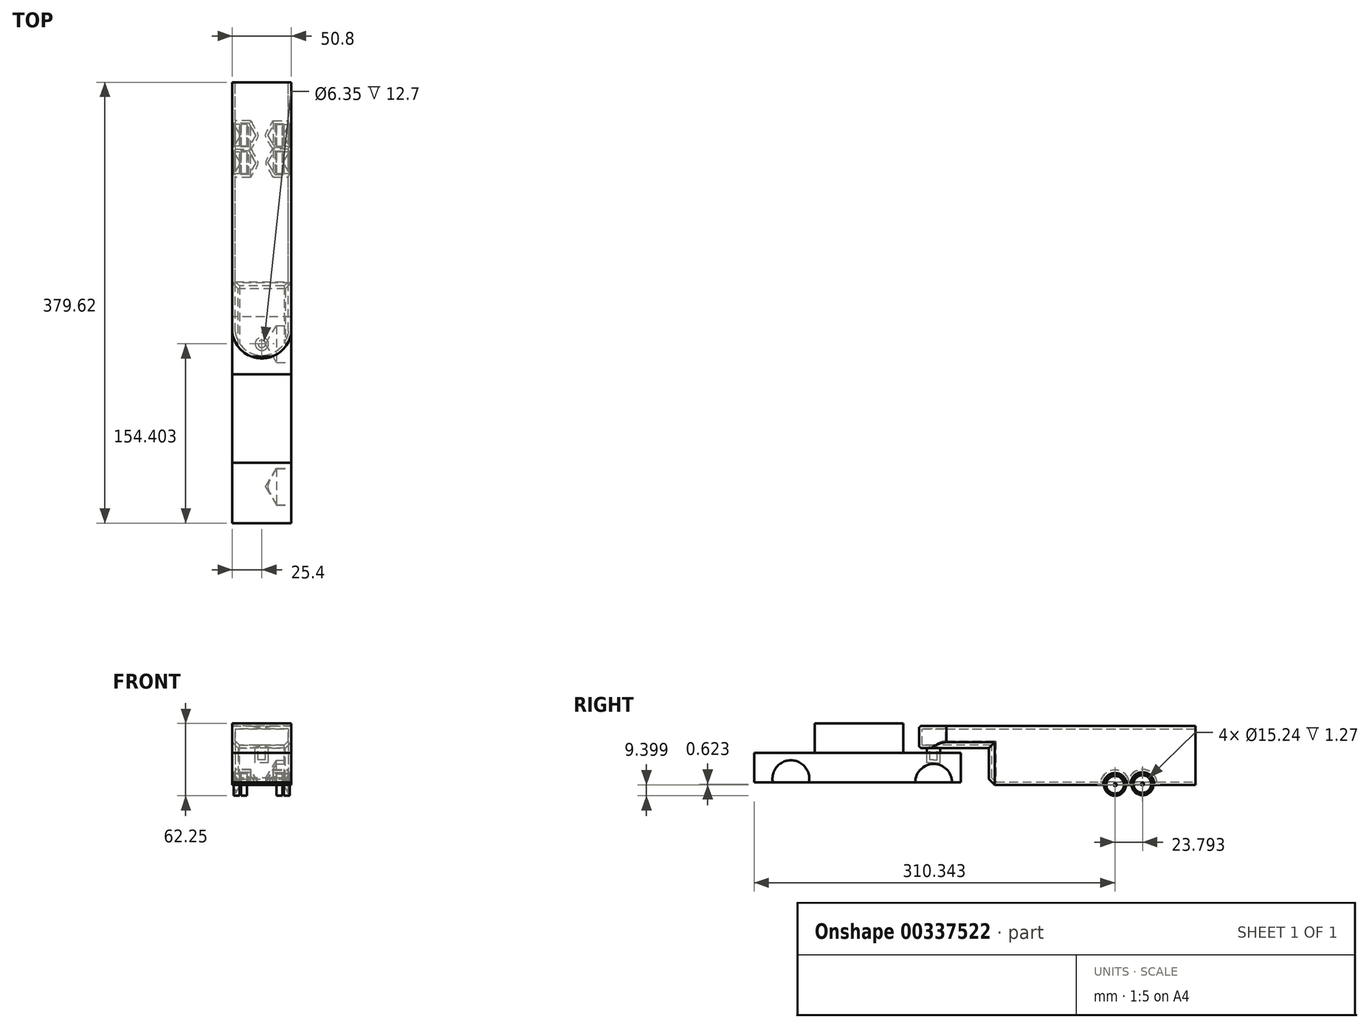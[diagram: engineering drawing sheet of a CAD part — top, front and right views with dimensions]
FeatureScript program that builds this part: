
annotation { "Feature Type Name" : "Feature", "Feature Type Description" : "" }
export const myFeature = defineFeature(function(context is Context, id is Id, definition is map)
    precondition{}
    {
        {
            var Q0;
            Q0=qCreatedBy(makeId("Right.planeOp"),FACE);
            var sketch = newSketch(context, id + "F0", { "sketchPlane" : qUnion([Q0])});
            skLineSegment(sketch, "E0.bottom", {"start": v(-60.47, 27.02) * mm, "end": v(117.33, 27.02) * mm});
            skLineSegment(sketch, "E0.top", {"start": v(-60.47, -23.78) * mm, "end": v(117.33, -23.78) * mm});
            skLineSegment(sketch, "E0.left", {"start": v(-60.47, 27.02) * mm, "end": v(-60.47, -23.78) * mm});
            skLineSegment(sketch, "E0.right", {"start": v(117.33, 27.02) * mm, "end": v(117.33, -23.78) * mm});
            skSolve(sketch);
        }
        {
            var Q0;
            Q0 = qSketchRegion(id + "F0", true);
            extrude(context, id + "F1", {"entities" : qUnion([Q0]), "endBound" : BoundingType.SYMMETRIC, "depth" : 50.8 * mm});
        }
        {
            var Q0;
            Q0=makeQuery(id+"F1.opExtrude","SWEPT_FACE",FACE,{"disambiguationData":[OSD([sQuery(id+"F0.wireOp",EDGE,"E0.bottom")])]});
            var sketch = newSketch(context, id + "F2", { "sketchPlane" : qUnion([Q0])});
            skLineSegment(sketch, "E1", {"start": v(25.4, -60.47) * mm, "end": v(25.4, -123.97) * mm});
            skLineSegment(sketch, "E2", {"start": v(25.4, -123.97) * mm, "end": v(-25.4, -123.97) * mm});
            skLineSegment(sketch, "E3", {"start": v(-25.4, -123.97) * mm, "end": v(-25.4, -60.47) * mm});
            skLineSegment(sketch, "E4", {"start": v(-25.4, -60.47) * mm, "end": v(25.4, -60.47) * mm});
            skSolve(sketch);
        }
        {
            var Q0;
            Q0 = qSketchRegion(id + "F2", true);
            extrude(context, id + "F3", {"entities" : qUnion([Q0]), "operationType" : NewBodyOperationType.ADD, "oppositeDirection" : true, "depth" : 19.05 * mm});
        }
        {
            var Q0;
            Q0=makeQuery(id+"F3.opExtrude","CAP_FACE",FACE,{"disambiguationData":[OSD([sQuery(id+"F2.wireOp",EDGE,"E1"),sQuery(id+"F2.wireOp",EDGE,"E2"),sQuery(id+"F2.wireOp",EDGE,"E3"),sQuery(id+"F2.wireOp",EDGE,"E4")])],"isStart":false});
            var sketch = newSketch(context, id + "F4", { "sketchPlane" : qUnion([Q0])});
            skCircle(sketch, "E5", {"center": v(0, 107.89) * mm, "radius": 5.72 * mm});
            skPoint(sketch, "E5.centerSnap0", {"position": v(25.4, 92.22) * mm});
            skPoint(sketch, "E5.centerSnap1", {"position": v(0, 60.47) * mm});
            skSolve(sketch);
        }
        {
            var Q0;
            Q0 = qSketchRegion(id + "F4", true);
            extrude(context, id + "F5", {"entities" : qUnion([Q0]), "operationType" : NewBodyOperationType.ADD, "depth" : 12.7 * mm});
        }
        {
            var Q0;
            Q0=makeQuery(id+"F3.opExtrude","SWEPT_EDGE",EDGE,{"disambiguationData":[OSD([sQuery(id+"F2.wireOp",EDGE,"E1"),sQuery(id+"F2.wireOp",EDGE,"E2")])]});
            var Q1;
            Q1=makeQuery(id+"F3.opExtrude","SWEPT_EDGE",EDGE,{"disambiguationData":[OSD([sQuery(id+"F2.wireOp",EDGE,"E2"),sQuery(id+"F2.wireOp",EDGE,"E3")])]});
            var Q2;
            Q2=makeQuery(id+"F1.opExtrude","CAP_EDGE",EDGE,{"disambiguationData":[OSD([sQuery(id+"F0.wireOp",EDGE,"E0.left")])],"isStart":false});
            var Q3;
            Q3=makeQuery(id+"F3.opExtrude","CAP_EDGE",EDGE,{"disambiguationData":[OSD([sQuery(id+"F2.wireOp",EDGE,"E1")])],"isStart":false});
            var Q4;
            Q4=makeQuery(id+"F3.opExtrude","CAP_EDGE",EDGE,{"disambiguationData":[OSD([sQuery(id+"F2.wireOp",EDGE,"E3")])],"isStart":false});
            var Q5;
            Q5=makeQuery(id+"F1.opExtrude","CAP_EDGE",EDGE,{"disambiguationData":[OSD([sQuery(id+"F0.wireOp",EDGE,"E0.left")])],"isStart":true});
            var Q6;
            Q6=makeQuery(id+"F1.opExtrude","SWEPT_EDGE",EDGE,{"disambiguationData":[OSD([sQuery(id+"F0.wireOp",EDGE,"E0.top"),sQuery(id+"F0.wireOp",EDGE,"E0.left")])]});
            var Q7;
            Q7=makeQuery(id+"F3.opExtrude","CAP_EDGE",EDGE,{"disambiguationData":[OSD([sQuery(id+"F2.wireOp",EDGE,"E2")])],"isStart":true});
            var Q8;
            Q8=makeQuery(id+"F3.opExtrude","SWEPT_FACE",FACE,{"disambiguationData":[OSD([sQuery(id+"F2.wireOp",EDGE,"E2")])]});
            chamfer(context, id + "F6", {"entities" : qUnion([Q0, Q1, Q2, Q3, Q4, Q5, Q6, Q7, Q8]), "width" : 5.08 * mm, "tangentPropagation" : true});
        }
        {
            var Q0;
            Q0=makeQuery(id+"F5.opExtrude","CAP_FACE",FACE,{"disambiguationData":[OSD([sQuery(id+"F4.wireOp",EDGE,"E5")])],"isStart":false});
            var sketch = newSketch(context, id + "F7", { "sketchPlane" : qUnion([Q0])});
            skCircle(sketch, "E6", {"center": v(0, 107.89) * mm, "radius": 2.54 * mm});
            skSolve(sketch);
        }
        {
            var Q0;
            Q0=makeQuery(id+"F3.boolean.opBoolean","MERGE",FACE,{"derivedFrom":[makeQuery(id+"F1.opExtrude","CAP_FACE",FACE,{"disambiguationData":[OSD([sQuery(id+"F0.wireOp",EDGE,"E0.bottom"),sQuery(id+"F0.wireOp",EDGE,"E0.top"),sQuery(id+"F0.wireOp",EDGE,"E0.left"),sQuery(id+"F0.wireOp",EDGE,"E0.right")])],"isStart":false}),makeQuery(id+"F3.opExtrude","SWEPT_FACE",FACE,{"disambiguationData":[OSD([sQuery(id+"F2.wireOp",EDGE,"E1")])]})]});
            var sketch = newSketch(context, id + "F8", { "sketchPlane" : qUnion([Q0])});
            skArc(sketch, "E7", {"start": v(57.9, -23.78) * mm, "mid": v(48.24, -14.02) * mm, "end": v(38.59, -23.78) * mm});
            skArc(sketch, "E8", {"start": v(81.4, -23.78) * mm, "mid": v(71.77, -13.4) * mm, "end": v(62.15, -23.78) * mm});
            skSolve(sketch);
        }
        {
            var Q0;
            Q0=sQuery(id+"F8.wireOp",VERTEX,"E7.center");
            var Q1;
            Q1=sQuery(id+"F8.wireOp",VERTEX,"E8.center");
            var Q2;
            Q2=makeQuery(id+"F1.opExtrude","SWEPT_BODY",BODY,{"disambiguationData":[OSD([sQuery(id+"F0.wireOp",EDGE,"E0.bottom"),sQuery(id+"F0.wireOp",EDGE,"E0.top"),sQuery(id+"F0.wireOp",EDGE,"E0.left"),sQuery(id+"F0.wireOp",EDGE,"E0.right")])]});
            hole(context, id + "F9", {"style" : HoleStyle.SIMPLE, "endStyle" : HoleEndStyle.BLIND, "holeDiameter" : 20.32 * mm, "holeDepth" : 14.22 * mm, "tappedDepth" : 12.7 * mm, "tapClearance" : 3, "locations" : qUnion([Q0, Q1]), "scope" : qUnion([Q2])});
        }
        {
            var Q0;
            Q0=makeQuery(id+"F3.boolean.opBoolean","MERGE",FACE,{"derivedFrom":[makeQuery(id+"F1.opExtrude","CAP_FACE",FACE,{"disambiguationData":[OSD([sQuery(id+"F0.wireOp",EDGE,"E0.bottom"),sQuery(id+"F0.wireOp",EDGE,"E0.top"),sQuery(id+"F0.wireOp",EDGE,"E0.left"),sQuery(id+"F0.wireOp",EDGE,"E0.right")])],"isStart":true}),makeQuery(id+"F3.opExtrude","SWEPT_FACE",FACE,{"disambiguationData":[OSD([sQuery(id+"F2.wireOp",EDGE,"E3")])]})]});
            var sketch = newSketch(context, id + "F10", { "sketchPlane" : qUnion([Q0])});
            skArc(sketch, "E9", {"start": v(-38.4, -23.78) * mm, "mid": v(-48.05, -13.97) * mm, "end": v(-57.7, -23.78) * mm});
            skArc(sketch, "E10", {"start": v(-62.2, -23.78) * mm, "mid": v(-71.85, -13.62) * mm, "end": v(-81.48, -23.78) * mm});
            skSolve(sketch);
        }
        {
            var Q0;
            Q0=sQuery(id+"F10.wireOp",VERTEX,"E10.center");
            var Q1;
            Q1=sQuery(id+"F10.wireOp",VERTEX,"E9.center");
            var Q2;
            Q2=makeQuery(id+"F1.opExtrude","SWEPT_BODY",BODY,{"disambiguationData":[OSD([sQuery(id+"F0.wireOp",EDGE,"E0.bottom"),sQuery(id+"F0.wireOp",EDGE,"E0.top"),sQuery(id+"F0.wireOp",EDGE,"E0.left"),sQuery(id+"F0.wireOp",EDGE,"E0.right")])]});
            hole(context, id + "F11", {"style" : HoleStyle.SIMPLE, "endStyle" : HoleEndStyle.BLIND, "holeDiameter" : 20.32 * mm, "holeDepth" : 14.22 * mm, "tappedDepth" : 12.7 * mm, "tapClearance" : 3, "locations" : qUnion([Q0, Q1]), "scope" : qUnion([Q2])});
        }
        {
            var Q0;
            Q0=makeQuery(id+"F3.boolean.opBoolean","MERGE",FACE,{"derivedFrom":[makeQuery(id+"F1.opExtrude","CAP_FACE",FACE,{"disambiguationData":[OSD([sQuery(id+"F0.wireOp",EDGE,"E0.bottom"),sQuery(id+"F0.wireOp",EDGE,"E0.top"),sQuery(id+"F0.wireOp",EDGE,"E0.left"),sQuery(id+"F0.wireOp",EDGE,"E0.right")])],"isStart":false}),makeQuery(id+"F3.opExtrude","SWEPT_FACE",FACE,{"disambiguationData":[OSD([sQuery(id+"F2.wireOp",EDGE,"E1")])]})]});
            var sketch = newSketch(context, id + "F12", { "sketchPlane" : qUnion([Q0])});
            skCircle(sketch, "E11", {"center": v(48.24, -23.67) * mm, "radius": 9.4 * mm});
            skCircle(sketch, "E12", {"center": v(71.77, -23.05) * mm, "radius": 9.4 * mm});
            skSolve(sketch);
        }
        {
            var Q0;
            Q0 = qSketchRegion(id + "F12", true);
            extrude(context, id + "F13", {"entities" : qUnion([Q0]), "oppositeDirection" : true, "depth" : 12.7 * mm, "hasSecondDirection" : true, "secondDirectionOppositeDirection" : true, "secondDirectionDepth" : 7.62 * mm});
        }
        {
            var Q0;
            Q0=makeQuery(id+"F3.boolean.opBoolean","MERGE",FACE,{"derivedFrom":[makeQuery(id+"F1.opExtrude","CAP_FACE",FACE,{"disambiguationData":[OSD([sQuery(id+"F0.wireOp",EDGE,"E0.bottom"),sQuery(id+"F0.wireOp",EDGE,"E0.top"),sQuery(id+"F0.wireOp",EDGE,"E0.left"),sQuery(id+"F0.wireOp",EDGE,"E0.right")])],"isStart":false}),makeQuery(id+"F3.opExtrude","SWEPT_FACE",FACE,{"disambiguationData":[OSD([sQuery(id+"F2.wireOp",EDGE,"E1")])]})]});
            var sketch = newSketch(context, id + "F14", { "sketchPlane" : qUnion([Q0])});
            skCircle(sketch, "E13", {"center": v(48.24, -23.67) * mm, "radius": 9.4 * mm});
            skCircle(sketch, "E14", {"center": v(71.77, -23.05) * mm, "radius": 9.4 * mm});
            skSolve(sketch);
        }
        {
            var Q0;
            Q0 = qSketchRegion(id + "F14", true);
            extrude(context, id + "F15", {"entities" : qUnion([Q0]), "oppositeDirection" : true, "depth" : 6.35 * mm, "hasSecondDirection" : true, "secondDirectionOppositeDirection" : true, "secondDirectionDepth" : 1.27 * mm});
        }
        {
            var Q0;
            Q0=makeQuery(id+"F3.boolean.opBoolean","MERGE",FACE,{"derivedFrom":[makeQuery(id+"F1.opExtrude","CAP_FACE",FACE,{"disambiguationData":[OSD([sQuery(id+"F0.wireOp",EDGE,"E0.bottom"),sQuery(id+"F0.wireOp",EDGE,"E0.top"),sQuery(id+"F0.wireOp",EDGE,"E0.left"),sQuery(id+"F0.wireOp",EDGE,"E0.right")])],"isStart":true}),makeQuery(id+"F3.opExtrude","SWEPT_FACE",FACE,{"disambiguationData":[OSD([sQuery(id+"F2.wireOp",EDGE,"E3")])]})]});
            var sketch = newSketch(context, id + "F16", { "sketchPlane" : qUnion([Q0])});
            skCircle(sketch, "E15", {"center": v(-71.85, -23.28) * mm, "radius": 9.4 * mm});
            skCircle(sketch, "E16", {"center": v(-48.05, -23.62) * mm, "radius": 9.4 * mm});
            skSolve(sketch);
        }
        {
            var Q0;
            Q0 = qSketchRegion(id + "F16", true);
            extrude(context, id + "F17", {"entities" : qUnion([Q0]), "oppositeDirection" : true, "depth" : 12.7 * mm, "hasSecondDirection" : true, "secondDirectionOppositeDirection" : true, "secondDirectionDepth" : 7.62 * mm});
        }
        {
            var Q0;
            Q0=makeQuery(id+"F3.boolean.opBoolean","MERGE",FACE,{"derivedFrom":[makeQuery(id+"F1.opExtrude","CAP_FACE",FACE,{"disambiguationData":[OSD([sQuery(id+"F0.wireOp",EDGE,"E0.bottom"),sQuery(id+"F0.wireOp",EDGE,"E0.top"),sQuery(id+"F0.wireOp",EDGE,"E0.left"),sQuery(id+"F0.wireOp",EDGE,"E0.right")])],"isStart":true}),makeQuery(id+"F3.opExtrude","SWEPT_FACE",FACE,{"disambiguationData":[OSD([sQuery(id+"F2.wireOp",EDGE,"E3")])]})]});
            var sketch = newSketch(context, id + "F18", { "sketchPlane" : qUnion([Q0])});
            skCircle(sketch, "E17", {"center": v(-71.85, -23.28) * mm, "radius": 9.4 * mm});
            skCircle(sketch, "E18", {"center": v(-48.05, -23.62) * mm, "radius": 9.4 * mm});
            skSolve(sketch);
        }
        {
            var Q0;
            Q0 = qSketchRegion(id + "F18", true);
            extrude(context, id + "F19", {"entities" : qUnion([Q0]), "oppositeDirection" : true, "depth" : 6.35 * mm, "hasSecondDirection" : true, "secondDirectionOppositeDirection" : true, "secondDirectionDepth" : 1.27 * mm});
        }
        {
            var Q0;
            Q0=sQuery(id+"F18.wireOp",VERTEX,"E18.center");
            var Q1;
            Q1=sQuery(id+"F18.wireOp",VERTEX,"E17.center");
            var Q2;
            Q2=sQuery(id+"F14.wireOp",VERTEX,"E13.center");
            var Q3;
            Q3=sQuery(id+"F14.wireOp",VERTEX,"E14.center");
            var Q4;
            Q4=makeQuery(id+"F19.opExtrude","SWEPT_BODY",BODY,{"disambiguationData":[OSD([sQuery(id+"F18.wireOp",EDGE,"E18")])]});
            var Q5;
            Q5=makeQuery(id+"F19.opExtrude","SWEPT_BODY",BODY,{"disambiguationData":[OSD([sQuery(id+"F18.wireOp",EDGE,"E17")])]});
            var Q6;
            Q6=makeQuery(id+"F15.opExtrude","SWEPT_BODY",BODY,{"disambiguationData":[OSD([sQuery(id+"F14.wireOp",EDGE,"E13")])]});
            var Q7;
            Q7=makeQuery(id+"F15.opExtrude","SWEPT_BODY",BODY,{"disambiguationData":[OSD([sQuery(id+"F14.wireOp",EDGE,"E14")])]});
            hole(context, id + "F20", {"style" : HoleStyle.SIMPLE, "endStyle" : HoleEndStyle.BLIND, "holeDiameter" : 15.24 * mm, "holeDepth" : 1.27 * mm, "tappedDepth" : 12.7 * mm, "tapClearance" : 3, "locations" : qUnion([Q0, Q1, Q2, Q3]), "scope" : qUnion([Q4, Q5, Q6, Q7])});
        }
        {
            var Q0;
            Q0=qCreatedBy(makeId("Right.planeOp"),FACE);
            var sketch = newSketch(context, id + "F21", { "sketchPlane" : qUnion([Q0])});
            skLineSegment(sketch, "E19", {"start": v(76.86, -33.73) * mm, "end": v(-278.52, -33.73) * mm});
            skLineSegment(sketch, "E20.bottom", {"start": v(-84.49, -21.67) * mm, "end": v(-135.29, -21.67) * mm});
            skLineSegment(sketch, "E20.top", {"start": v(-84.49, 3.73) * mm, "end": v(-135.29, 3.73) * mm});
            skLineSegment(sketch, "E20.left", {"start": v(-84.49, -21.67) * mm, "end": v(-84.49, 3.73) * mm});
            skLineSegment(sketch, "E20.right", {"start": v(-135.29, -21.67) * mm, "end": v(-135.29, 3.73) * mm});
            skLineSegment(sketch, "E21.bottom", {"start": v(-135.29, 3.73) * mm, "end": v(-211.49, 3.73) * mm});
            skLineSegment(sketch, "E21.top", {"start": v(-135.29, -21.67) * mm, "end": v(-211.49, -21.67) * mm});
            skLineSegment(sketch, "E21.left", {"start": v(-135.29, 3.73) * mm, "end": v(-135.29, -21.67) * mm});
            skLineSegment(sketch, "E21.right", {"start": v(-211.49, 3.73) * mm, "end": v(-211.49, -21.67) * mm});
            skLineSegment(sketch, "E22.bottom", {"start": v(-211.49, 3.73) * mm, "end": v(-262.29, 3.73) * mm});
            skLineSegment(sketch, "E22.top", {"start": v(-211.49, -21.67) * mm, "end": v(-262.29, -21.67) * mm});
            skLineSegment(sketch, "E22.right", {"start": v(-262.29, 3.73) * mm, "end": v(-262.29, -21.67) * mm});
            skSolve(sketch);
        }
        {
            var Q0;
            Q0 = qSketchRegion(id + "F21", true);
            extrude(context, id + "F22", {"entities" : qUnion([Q0]), "endBound" : BoundingType.SYMMETRIC, "depth" : 50.8 * mm});
        }
        {
            var Q0;
            Q0=qCreatedBy(makeId("Right.planeOp"),FACE);
            var sketch = newSketch(context, id + "F23", { "sketchPlane" : qUnion([Q0])});
            skLineSegment(sketch, "E23.bottom", {"start": v(-210.17, 3.78) * mm, "end": v(-133.97, 3.78) * mm});
            skLineSegment(sketch, "E23.top", {"start": v(-210.17, 29.18) * mm, "end": v(-133.97, 29.18) * mm});
            skLineSegment(sketch, "E23.left", {"start": v(-210.17, 3.78) * mm, "end": v(-210.17, 29.18) * mm});
            skLineSegment(sketch, "E23.right", {"start": v(-133.97, 3.78) * mm, "end": v(-133.97, 29.18) * mm});
            skSolve(sketch);
        }
        {
            var Q0;
            Q0 = qSketchRegion(id + "F23", true);
            extrude(context, id + "F24", {"entities" : qUnion([Q0]), "endBound" : BoundingType.SYMMETRIC, "depth" : 50.8 * mm});
        }
        {
            var Q0;
            Q0=makeQuery(id+"F22.opExtrude","CAP_FACE",FACE,{"disambiguationData":[OSD([sQuery(id+"F21.wireOp",EDGE,"E20.bottom"),sQuery(id+"F21.wireOp",EDGE,"E20.top"),sQuery(id+"F21.wireOp",EDGE,"E20.left"),sQuery(id+"F21.wireOp",EDGE,"E21.bottom"),sQuery(id+"F21.wireOp",EDGE,"E21.top"),sQuery(id+"F21.wireOp",EDGE,"E22.bottom"),sQuery(id+"F21.wireOp",EDGE,"E22.top"),sQuery(id+"F21.wireOp",EDGE,"E22.right")])],"isStart":false});
            var sketch = newSketch(context, id + "F25", { "sketchPlane" : qUnion([Q0])});
            skArc(sketch, "E24", {"start": v(-215.91, -21.67) * mm, "mid": v(-230.81, -3.21) * mm, "end": v(-245.7, -21.67) * mm});
            skArc(sketch, "E25", {"start": v(-92.67, -21.67) * mm, "mid": v(-107.9, -6.43) * mm, "end": v(-123.15, -21.67) * mm});
            skSolve(sketch);
        }
        {
            var Q0;
            Q0=makeQuery(id+"F3.boolean.opBoolean","MERGE",FACE,{"derivedFrom":[makeQuery(id+"F1.opExtrude","SWEPT_FACE",FACE,{"disambiguationData":[OSD([sQuery(id+"F0.wireOp",EDGE,"E0.bottom")])]}),makeQuery(id+"F3.opExtrude","CAP_FACE",FACE,{"disambiguationData":[OSD([sQuery(id+"F2.wireOp",EDGE,"E1"),sQuery(id+"F2.wireOp",EDGE,"E2"),sQuery(id+"F2.wireOp",EDGE,"E3"),sQuery(id+"F2.wireOp",EDGE,"E4")])],"isStart":true})]});
            var sketch = newSketch(context, id + "F26", { "sketchPlane" : qUnion([Q0])});
            skArc(sketch, "E26", {"start": v(-25.4, -91.94) * mm, "mid": v(-0.42, -120.35) * mm, "end": v(25.4, -92.71) * mm});
            skLineSegment(sketch, "E27", {"start": v(-25.4, -91.94) * mm, "end": v(-81.95, -91.94) * mm});
            skLineSegment(sketch, "E28", {"start": v(-81.95, -91.94) * mm, "end": v(-34.4, -125.6) * mm});
            skLineSegment(sketch, "E29", {"start": v(-34.4, -125.6) * mm, "end": v(33.43, -125.6) * mm});
            skLineSegment(sketch, "E30", {"start": v(33.43, -125.6) * mm, "end": v(33.43, -87.73) * mm});
            skLineSegment(sketch, "E31", {"start": v(33.43, -87.73) * mm, "end": v(25.4, -92.71) * mm});
            skSolve(sketch);
        }
        {
            var Q0;
            Q0 = qSketchRegion(id + "F26", true);
            var Q1;
            Q1=makeQuery(id+"F22.opExtrude","SWEPT_FACE",FACE,{"disambiguationData":[OSD([sQuery(id+"F21.wireOp",EDGE,"E20.top"),sQuery(id+"F21.wireOp",EDGE,"E21.bottom"),sQuery(id+"F21.wireOp",EDGE,"E22.bottom")])]});
            extrude(context, id + "F27", {"entities" : qUnion([Q0]), "operationType" : NewBodyOperationType.REMOVE, "endBound" : BoundingType.UP_TO_SURFACE, "oppositeDirection" : true, "endBoundEntityFace" : qUnion([Q1]), "depth" : 25.4 * mm});
        }
        {
            var Q0;
            Q0=makeQuery(id+"F1.opExtrude","SWEPT_FACE",FACE,{"disambiguationData":[OSD([sQuery(id+"F0.wireOp",EDGE,"E0.right")])]});
            shell(context, id + "F28", {"entities" : qUnion([Q0]), "thickness" : 2.54 * mm});
        }
        {
            var Q0;
            Q0=sQuery(id+"F25.wireOp",VERTEX,"E25.center");
            var Q1;
            Q1=sQuery(id+"F25.wireOp",VERTEX,"E24.center");
            var Q2;
            Q2=makeQuery(id+"F22.opExtrude","SWEPT_BODY",BODY,{"disambiguationData":[OSD([sQuery(id+"F21.wireOp",EDGE,"E20.bottom"),sQuery(id+"F21.wireOp",EDGE,"E20.top"),sQuery(id+"F21.wireOp",EDGE,"E20.left"),sQuery(id+"F21.wireOp",EDGE,"E21.bottom"),sQuery(id+"F21.wireOp",EDGE,"E21.top"),sQuery(id+"F21.wireOp",EDGE,"E22.bottom"),sQuery(id+"F21.wireOp",EDGE,"E22.top"),sQuery(id+"F21.wireOp",EDGE,"E22.right")])]});
            hole(context, id + "F29", {"style" : HoleStyle.SIMPLE, "endStyle" : HoleEndStyle.BLIND, "holeDiameter" : 31.75 * mm, "holeDepth" : 12.7 * mm, "tappedDepth" : 12.7 * mm, "tapClearance" : 3, "locations" : qUnion([Q0, Q1]), "scope" : qUnion([Q2])});
        }
    });
